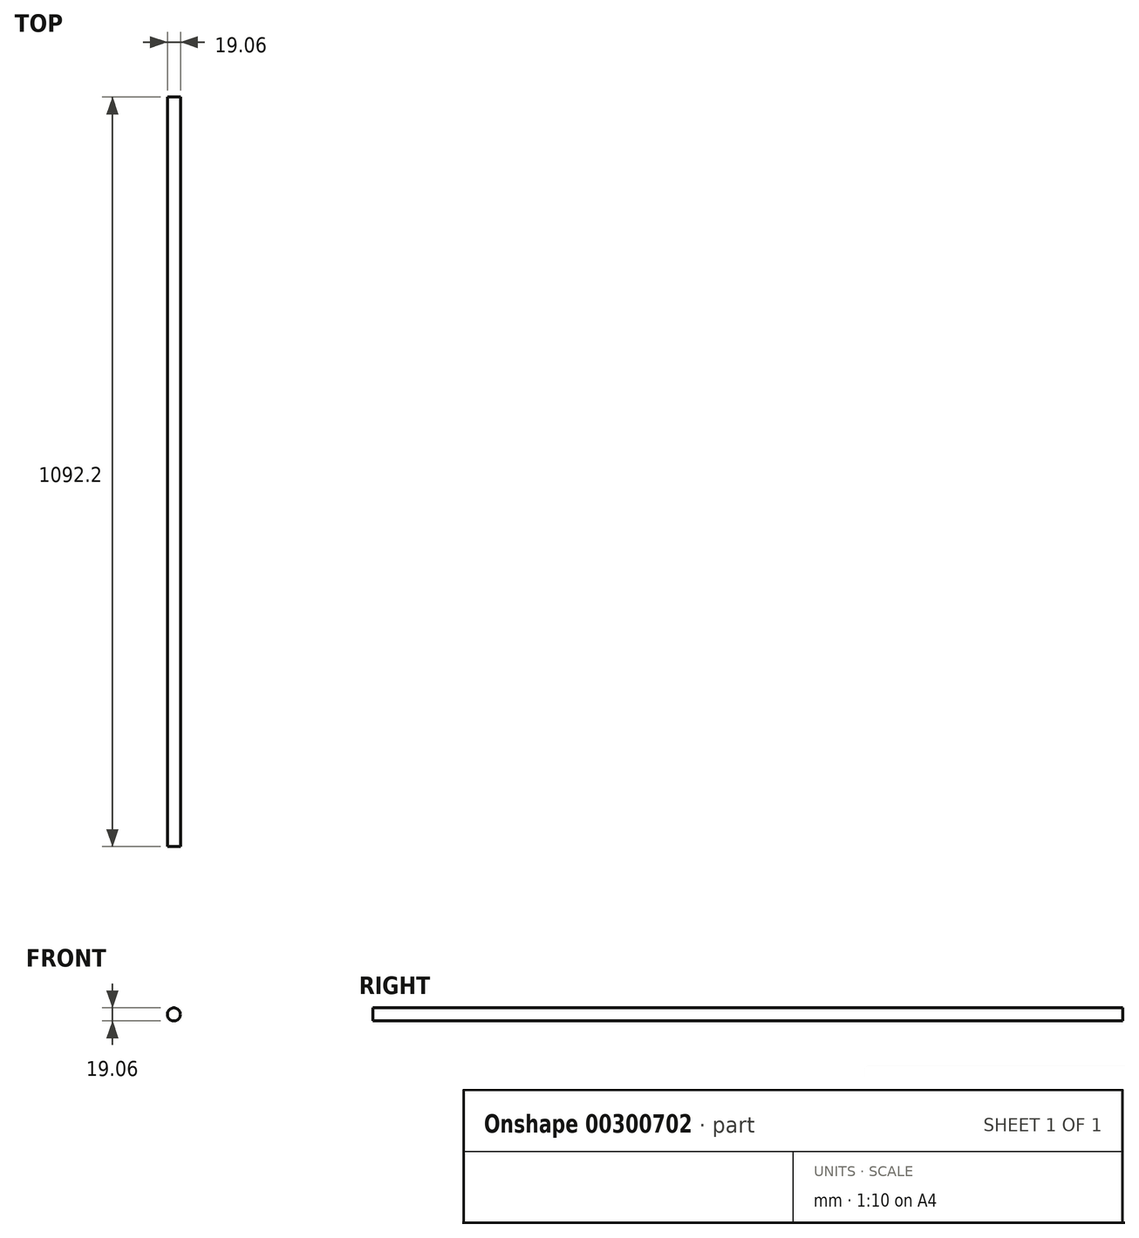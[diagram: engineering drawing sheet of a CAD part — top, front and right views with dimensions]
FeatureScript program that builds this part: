
annotation { "Feature Type Name" : "Feature", "Feature Type Description" : "" }
export const myFeature = defineFeature(function(context is Context, id is Id, definition is map)
    precondition{}
    {
        {
            var Q0;
            Q0=qCreatedBy(makeId("Front.planeOp"),FACE);
            var sketch = newSketch(context, id + "F0", { "sketchPlane" : qUnion([Q0])});
            skCircle(sketch, "E0", {"center": v(0, 0) * mm, "radius": 9.53 * mm});
            skSolve(sketch);
        }
        {
            var Q0;
            Q0=makeQuery(id+"F0.imprint","IMPRINT",FACE,{"disambiguationData":[TD([[makeQuery(id+"F0.imprint","IMPRINT",EDGE,{"derivedFrom":sQuery(id+"F0.wireOp",EDGE,"E0")}),1.0]])]});
            extrude(context, id + "F1", {"entities" : qUnion([Q0]), "depth" : 1092.2 * mm});
        }
    });
